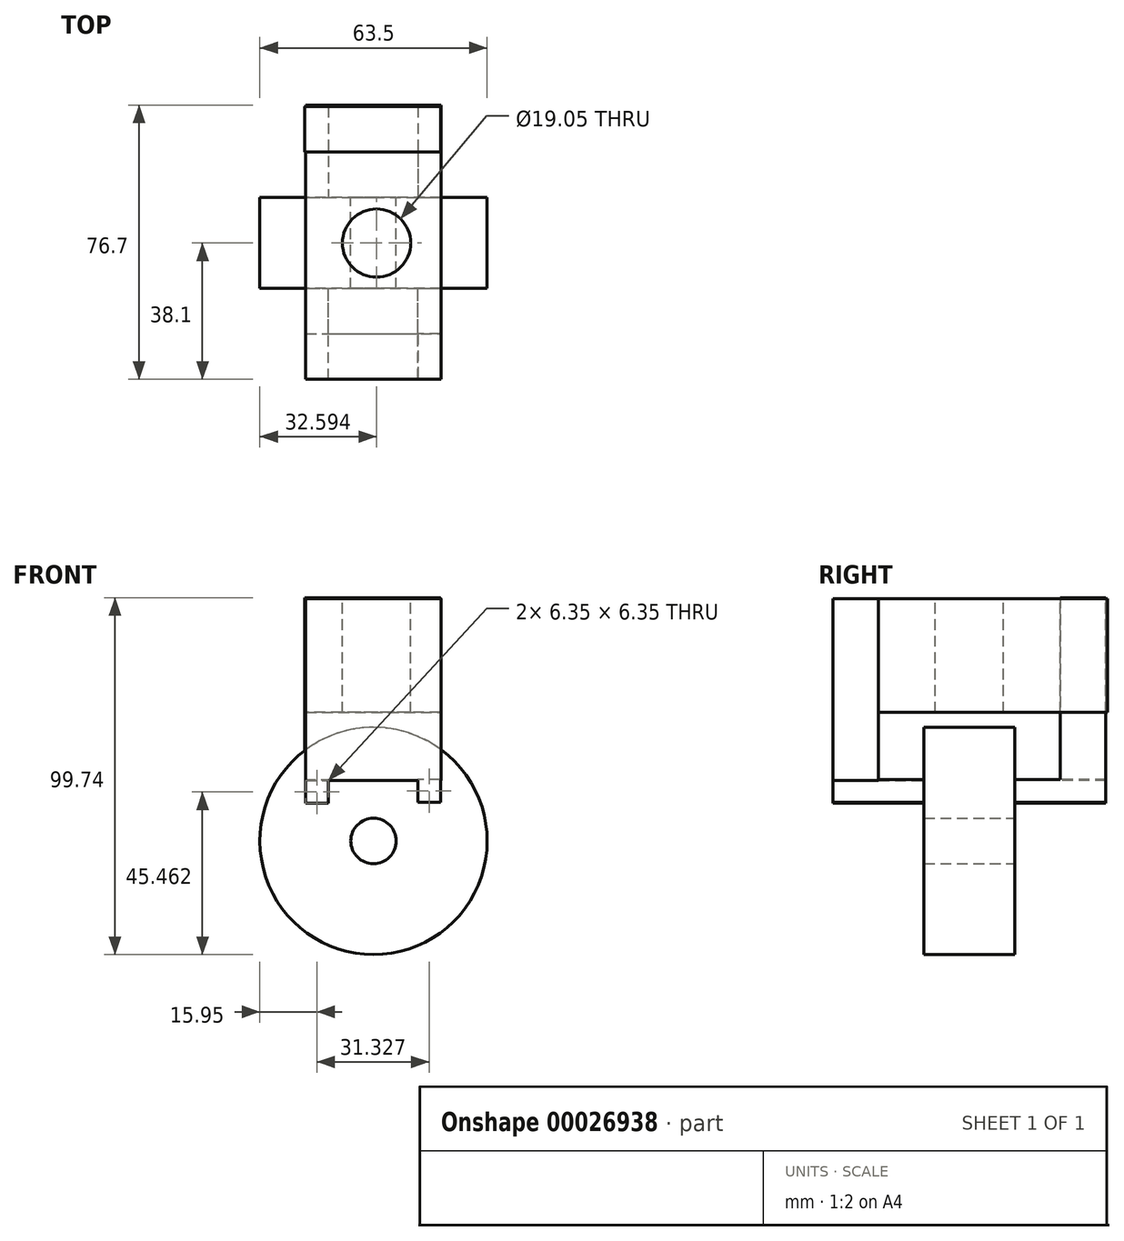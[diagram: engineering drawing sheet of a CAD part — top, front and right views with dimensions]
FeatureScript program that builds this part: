
annotation { "Feature Type Name" : "Feature", "Feature Type Description" : "" }
export const myFeature = defineFeature(function(context is Context, id is Id, definition is map)
    precondition{}
    {
        {
            var Q0;
            Q0=qCreatedBy(makeId("Front.planeOp"),FACE);
            var sketch = newSketch(context, id + "F0", { "sketchPlane" : qUnion([Q0])});
            skCircle(sketch, "E0", {"center": v(-36.54, 25.95) * mm, "radius": 31.75 * mm});
            skCircle(sketch, "E1", {"center": v(-36.54, 25.95) * mm, "radius": 6.35 * mm});
            skLineSegment(sketch, "E2.bottom", {"start": v(-55.51, 42.84) * mm, "end": v(-49.16, 42.84) * mm});
            skLineSegment(sketch, "E2.top", {"start": v(-55.51, 36.49) * mm, "end": v(-49.16, 36.49) * mm});
            skLineSegment(sketch, "E2.left", {"start": v(-55.51, 42.84) * mm, "end": v(-55.51, 36.49) * mm});
            skLineSegment(sketch, "E2.right", {"start": v(-49.16, 42.84) * mm, "end": v(-49.16, 36.49) * mm});
            skLineSegment(sketch, "E3.bottom", {"start": v(-24.19, 43.14) * mm, "end": v(-17.84, 43.14) * mm});
            skLineSegment(sketch, "E3.top", {"start": v(-24.19, 36.79) * mm, "end": v(-17.84, 36.79) * mm});
            skLineSegment(sketch, "E3.left", {"start": v(-24.19, 43.14) * mm, "end": v(-24.19, 36.79) * mm});
            skLineSegment(sketch, "E3.right", {"start": v(-17.84, 43.14) * mm, "end": v(-17.84, 36.79) * mm});
            skSolve(sketch);
        }
        {
            var Q0;
            Q0=makeQuery(id+"F0.imprint","IMPRINT",FACE,{"disambiguationData":[TD([[makeQuery(id+"F0.imprint","IMPRINT",EDGE,{"derivedFrom":sQuery(id+"F0.wireOp",EDGE,"E0")}),1.0]])]});
            extrude(context, id + "F1", {"entities" : qUnion([Q0]), "depth" : 25.4 * mm});
        }
        {
            var Q0;
            Q0=makeQuery(id+"F0.imprint","IMPRINT",FACE,{"disambiguationData":[TD([[makeQuery(id+"F0.imprint","IMPRINT",EDGE,{"derivedFrom":sQuery(id+"F0.wireOp",EDGE,"E2.bottom")}),-1.0]])]});
            extrude(context, id + "F2", {"entities" : qUnion([Q0]), "operationType" : NewBodyOperationType.ADD, "depth" : 50.8 * mm});
        }
        {
            var Q0;
            Q0=makeQuery(id+"F0.imprint","IMPRINT",FACE,{"disambiguationData":[TD([[makeQuery(id+"F0.imprint","IMPRINT",EDGE,{"derivedFrom":sQuery(id+"F0.wireOp",EDGE,"E2.bottom")}),-1.0]])]});
            extrude(context, id + "F3", {"entities" : qUnion([Q0]), "operationType" : NewBodyOperationType.ADD, "oppositeDirection" : true, "depth" : 25.4 * mm});
        }
        {
            var Q0;
            Q0=makeQuery(id+"F0.imprint","IMPRINT",FACE,{"disambiguationData":[TD([[makeQuery(id+"F0.imprint","IMPRINT",EDGE,{"derivedFrom":sQuery(id+"F0.wireOp",EDGE,"E3.bottom")}),-1.0]])]});
            extrude(context, id + "F4", {"entities" : qUnion([Q0]), "operationType" : NewBodyOperationType.ADD, "depth" : 50.8 * mm});
        }
        {
            var Q0;
            Q0=makeQuery(id+"F0.imprint","IMPRINT",FACE,{"disambiguationData":[TD([[makeQuery(id+"F0.imprint","IMPRINT",EDGE,{"derivedFrom":sQuery(id+"F0.wireOp",EDGE,"E3.bottom")}),-1.0]])]});
            extrude(context, id + "F5", {"entities" : qUnion([Q0]), "operationType" : NewBodyOperationType.ADD, "oppositeDirection" : true, "depth" : 25.4 * mm});
        }
        {
            var Q0;
            Q0=makeQuery(id+"F2.opExtrude","SWEPT_FACE",FACE,{"disambiguationData":[OSD([sQuery(id+"F0.wireOp",EDGE,"E2.bottom")])]});
            var sketch = newSketch(context, id + "F6", { "sketchPlane" : qUnion([Q0])});
            skLineSegment(sketch, "E4", {"start": v(-55.51, -50.8) * mm, "end": v(-55.51, -50.8) * mm});
            skLineSegment(sketch, "E5", {"start": v(-17.65, -40) * mm, "end": v(-17.65, -50.8) * mm});
            skLineSegment(sketch, "E6", {"start": v(-55.51, -50.8) * mm, "end": v(-17.65, -50.8) * mm});
            skLineSegment(sketch, "E7", {"start": v(-55.51, -38.1) * mm, "end": v(-17.65, -38.1) * mm});
            skLineSegment(sketch, "E8", {"start": v(-55.51, -50.8) * mm, "end": v(-55.51, -38.1) * mm});
            skLineSegment(sketch, "E9", {"start": v(-17.65, -40) * mm, "end": v(-17.65, -38.1) * mm});
            skLineSegment(sketch, "E10", {"start": v(-17.65, -38.1) * mm, "end": v(-55.51, -38.1) * mm});
            skLineSegment(sketch, "E11", {"start": v(-23.87, -38.1) * mm, "end": v(-17.65, -38.1) * mm});
            skSolve(sketch);
        }
        {
            var Q0;
            {var subQ6=sQuery(id+"F6.wireOp",EDGE,"E5");Q0=makeQuery(id+"F6.imprint","IMPRINT",FACE,{"disambiguationData":[TD([[makeQuery(id+"F6.imprint","IMPRINT",EDGE,{"derivedFrom":subQ6}),-1.0]])]});}
            var Q1;
            {var subQ6=sQuery(id+"F6.wireOp",EDGE,"E8");Q1=makeQuery(id+"F6.imprint","IMPRINT",FACE,{"disambiguationData":[TD([[makeQuery(id+"F6.imprint","IMPRINT",EDGE,{"derivedFrom":subQ6}),-1.0]])]});}
            extrude(context, id + "F7", {"entities" : qUnion([Q0, Q1]), "operationType" : NewBodyOperationType.ADD, "depth" : 25.4 * mm});
        }
        {
            var Q0;
            Q0=makeQuery(id+"F5.opExtrude","SWEPT_FACE",FACE,{"disambiguationData":[OSD([sQuery(id+"F0.wireOp",EDGE,"E3.bottom")])]});
            var sketch = newSketch(context, id + "F8", { "sketchPlane" : qUnion([Q0])});
            skLineSegment(sketch, "E12.bottom", {"start": v(-17.84, 25.4) * mm, "end": v(-55.74, 25.4) * mm});
            skLineSegment(sketch, "E12.top", {"start": v(-17.84, 12.7) * mm, "end": v(-55.74, 12.7) * mm});
            skLineSegment(sketch, "E12.left", {"start": v(-17.84, 25.4) * mm, "end": v(-17.84, 12.7) * mm});
            skLineSegment(sketch, "E12.right", {"start": v(-55.74, 25.4) * mm, "end": v(-55.74, 12.7) * mm});
            skSolve(sketch);
        }
        {
            var Q0;
            {var subQ6=sQuery(id+"F8.wireOp",EDGE,"E12.left");Q0=makeQuery(id+"F8.imprint","IMPRINT",FACE,{"disambiguationData":[TD([[makeQuery(id+"F8.imprint","IMPRINT",EDGE,{"derivedFrom":subQ6}),-1.0]])]});}
            var Q1;
            {var subQ5=sQuery(id+"F8.wireOp",EDGE,"E12.right");Q1=makeQuery(id+"F8.imprint","IMPRINT",FACE,{"disambiguationData":[TD([[makeQuery(id+"F8.imprint","IMPRINT",EDGE,{"derivedFrom":subQ5}),1.0]])]});}
            extrude(context, id + "F9", {"entities" : qUnion([Q0, Q1]), "operationType" : NewBodyOperationType.ADD, "depth" : 25.4 * mm});
        }
        {
            var Q0;
            Q0=makeQuery(id+"F7.opExtrude","CAP_FACE",FACE,{"disambiguationData":[OSD([sQuery(id+"F6.wireOp",EDGE,"E5"),sQuery(id+"F6.wireOp",EDGE,"E6"),sQuery(id+"F6.wireOp",EDGE,"E9"),sQuery(id+"F6.wireOp",EDGE,"E10"),sQuery(id+"F6.wireOp",EDGE,"E8"),sQuery(id+"F6.wireOp",EDGE,"E11")])],"isStart":false});
            var sketch = newSketch(context, id + "F10", { "sketchPlane" : qUnion([Q0])});
            skLineSegment(sketch, "E13.bottom", {"start": v(-55.51, -50.8) * mm, "end": v(-17.7, -50.8) * mm});
            skLineSegment(sketch, "E13.top", {"start": v(-55.51, 25.9) * mm, "end": v(-17.7, 25.9) * mm});
            skLineSegment(sketch, "E13.left", {"start": v(-55.51, -50.8) * mm, "end": v(-55.51, 25.9) * mm});
            skLineSegment(sketch, "E13.right", {"start": v(-17.7, -50.8) * mm, "end": v(-17.7, 25.9) * mm});
            skCircle(sketch, "E14", {"center": v(-35.7, -12.7) * mm, "radius": 9.53 * mm});
            skSolve(sketch);
        }
        {
            var Q0;
            {var subQ5=sQuery(id+"F10.wireOp",EDGE,"E13.top");Q0=makeQuery(id+"F10.imprint","IMPRINT",FACE,{"disambiguationData":[TD([[makeQuery(id+"F10.imprint","IMPRINT",EDGE,{"derivedFrom":subQ5}),-1.0]])]});}
            var Q1;
            {var subQ5=sQuery(id+"F10.wireOp",EDGE,"E13.bottom");Q1=makeQuery(id+"F10.imprint","IMPRINT",FACE,{"disambiguationData":[TD([[makeQuery(id+"F10.imprint","IMPRINT",EDGE,{"derivedFrom":subQ5}),1.0]])]});}
            extrude(context, id + "F11", {"entities" : qUnion([Q0, Q1]), "operationType" : NewBodyOperationType.ADD, "oppositeDirection" : true, "depth" : 6.35 * mm});
        }
        {
            var Q0;
            Q0=makeQuery(id+"F11.boolean.opBoolean","MERGE",FACE,{"derivedFrom":[makeQuery(id+"F7.opExtrude","CAP_FACE",FACE,{"disambiguationData":[OSD([sQuery(id+"F6.wireOp",EDGE,"E5"),sQuery(id+"F6.wireOp",EDGE,"E6"),sQuery(id+"F6.wireOp",EDGE,"E9"),sQuery(id+"F6.wireOp",EDGE,"E10"),sQuery(id+"F6.wireOp",EDGE,"E8"),sQuery(id+"F6.wireOp",EDGE,"E11")])],"isStart":false}),makeQuery(id+"F11.opExtrude","CAP_FACE",FACE,{"disambiguationData":[OSD([sQuery(id+"F10.wireOp",EDGE,"E13.bottom"),sQuery(id+"F10.wireOp",EDGE,"E13.top"),sQuery(id+"F10.wireOp",EDGE,"E13.left"),sQuery(id+"F10.wireOp",EDGE,"E13.right")])],"isStart":true})]});
            var Q1;
            Q1=makeQuery(id+"F9.opExtrude","CAP_FACE",FACE,{"disambiguationData":[OSD([sQuery(id+"F8.wireOp",EDGE,"E12.bottom"),sQuery(id+"F8.wireOp",EDGE,"E12.top"),sQuery(id+"F8.wireOp",EDGE,"E12.left"),sQuery(id+"F8.wireOp",EDGE,"E12.right")])],"isStart":false});
            extrude(context, id + "F12", {"entities" : qUnion([Q0, Q1]), "operationType" : NewBodyOperationType.ADD, "depth" : 25.4 * mm});
        }
    });
